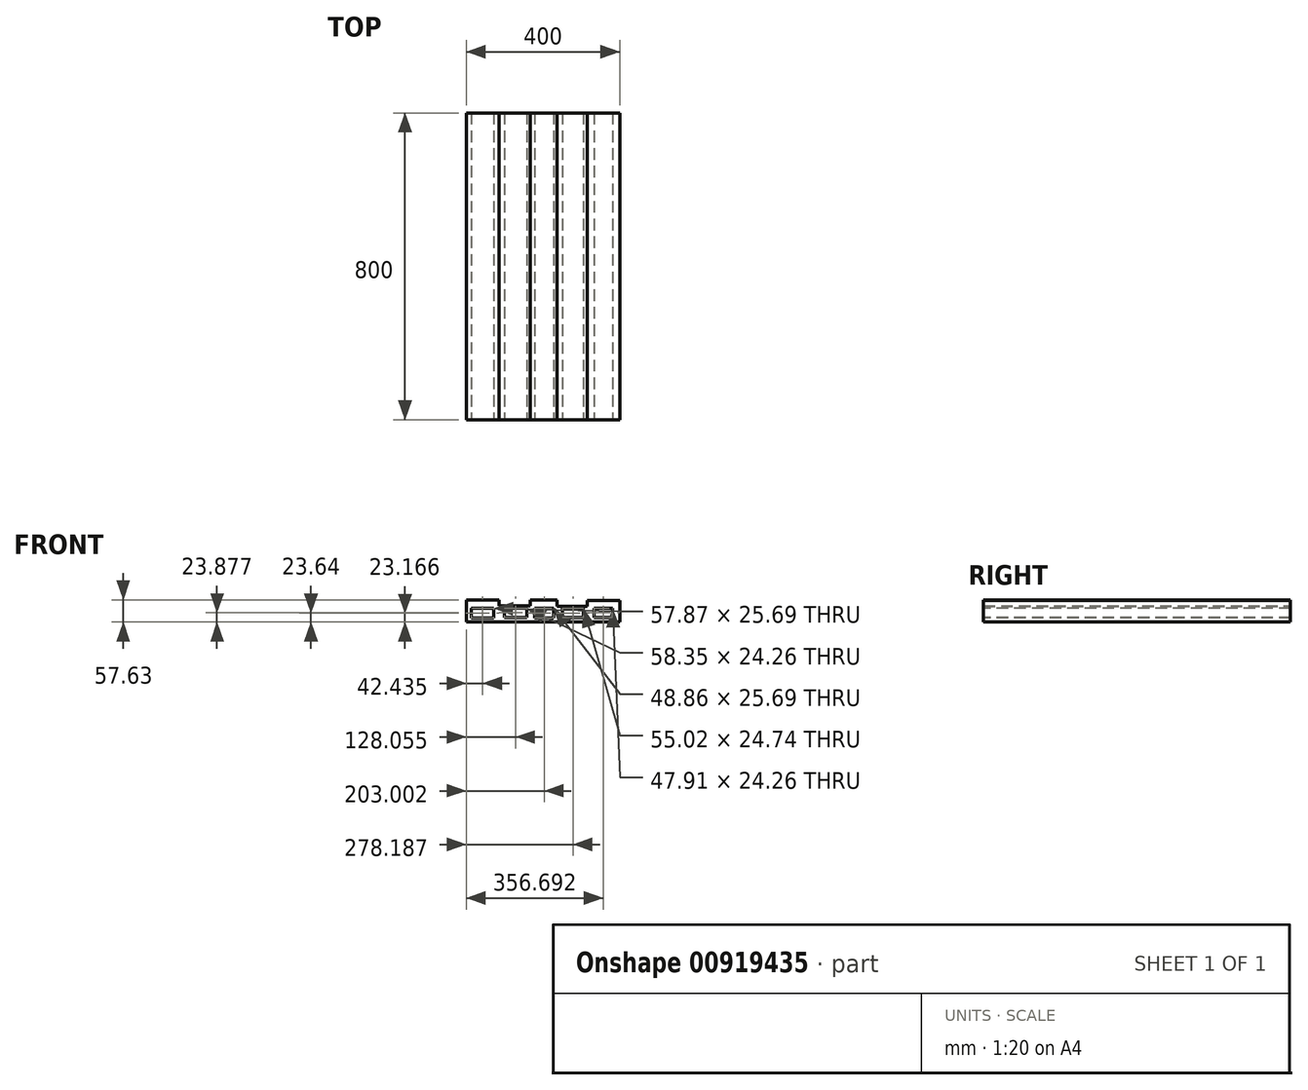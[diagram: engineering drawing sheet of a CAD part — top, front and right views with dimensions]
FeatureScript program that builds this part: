
annotation { "Feature Type Name" : "Feature", "Feature Type Description" : "" }
export const myFeature = defineFeature(function(context is Context, id is Id, definition is map)
    precondition{}
    {
        {
            var Q0;
            Q0=qCreatedBy(makeId("Front.planeOp"),FACE);
            var sketch = newSketch(context, id + "F0", { "sketchPlane" : qUnion([Q0])});
            skLineSegment(sketch, "E0.bottom", {"start": v(-56.77, 21.62) * mm, "end": v(28.15, 21.62) * mm});
            skLineSegment(sketch, "E0.top", {"start": v(-56.77, -36) * mm, "end": v(28.15, -36) * mm});
            skLineSegment(sketch, "E0.left", {"start": v(-56.77, 21.62) * mm, "end": v(-56.77, -36) * mm});
            skLineSegment(sketch, "E0.right", {"start": v(28.15, 21.62) * mm, "end": v(28.15, -36) * mm});
            skLineSegment(sketch, "E1.bottom", {"start": v(28.15, 5.48) * mm, "end": v(110.29, 5.48) * mm});
            skLineSegment(sketch, "E1.top", {"start": v(28.15, -36) * mm, "end": v(110.29, -36) * mm});
            skLineSegment(sketch, "E1.left", {"start": v(28.15, 5.48) * mm, "end": v(28.15, -36) * mm});
            skLineSegment(sketch, "E1.right", {"start": v(110.29, 5.48) * mm, "end": v(110.29, -36) * mm});
            skLineSegment(sketch, "E2.bottom", {"start": v(110.29, 21.62) * mm, "end": v(180.17, 21.62) * mm});
            skLineSegment(sketch, "E2.top", {"start": v(110.29, -36) * mm, "end": v(180.17, -36) * mm});
            skLineSegment(sketch, "E2.left", {"start": v(110.29, 21.62) * mm, "end": v(110.29, -36) * mm});
            skLineSegment(sketch, "E2.right", {"start": v(180.17, 21.62) * mm, "end": v(180.17, -36) * mm});
            skLineSegment(sketch, "E3.bottom", {"start": v(180.17, -36) * mm, "end": v(258.18, -36) * mm});
            skLineSegment(sketch, "E3.top", {"start": v(180.17, 4.79) * mm, "end": v(258.18, 4.79) * mm});
            skLineSegment(sketch, "E3.left", {"start": v(180.17, -36) * mm, "end": v(180.17, 4.79) * mm});
            skLineSegment(sketch, "E3.right", {"start": v(258.18, -36) * mm, "end": v(258.18, 4.79) * mm});
            skLineSegment(sketch, "E4.bottom", {"start": v(258.18, 19.75) * mm, "end": v(343.23, 19.75) * mm});
            skLineSegment(sketch, "E4.top", {"start": v(258.18, -36) * mm, "end": v(343.23, -36) * mm});
            skLineSegment(sketch, "E4.left", {"start": v(258.18, 19.75) * mm, "end": v(258.18, -36) * mm});
            skLineSegment(sketch, "E4.right", {"start": v(343.23, 19.75) * mm, "end": v(343.23, -36) * mm});
            skSolve(sketch);
        }
        {
            var Q0;
            Q0 = qSketchRegion(id + "F0", true);
            extrude(context, id + "F1", {"entities" : qUnion([Q0]), "depth" : 800 * mm, "offsetDistance" : 25 * mm});
        }
        {
            var Q0;
            Q0=makeQuery(id+"F1.opExtrude","CAP_FACE",FACE,{"disambiguationData":[OSD([sQuery(id+"F0.wireOp",EDGE,"E0.bottom"),sQuery(id+"F0.wireOp",EDGE,"E0.top"),sQuery(id+"F0.wireOp",EDGE,"E0.left"),sQuery(id+"F0.wireOp",EDGE,"E0.right"),sQuery(id+"F0.wireOp",EDGE,"E1.bottom"),sQuery(id+"F0.wireOp",EDGE,"E1.top"),sQuery(id+"F0.wireOp",EDGE,"E2.bottom"),sQuery(id+"F0.wireOp",EDGE,"E2.top"),sQuery(id+"F0.wireOp",EDGE,"E2.left"),sQuery(id+"F0.wireOp",EDGE,"E2.right"),sQuery(id+"F0.wireOp",EDGE,"E3.bottom"),sQuery(id+"F0.wireOp",EDGE,"E3.top"),sQuery(id+"F0.wireOp",EDGE,"E4.bottom"),sQuery(id+"F0.wireOp",EDGE,"E4.top"),sQuery(id+"F0.wireOp",EDGE,"E4.left"),sQuery(id+"F0.wireOp",EDGE,"E4.right")])],"isStart":false});
            var sketch = newSketch(context, id + "F2", { "sketchPlane" : qUnion([Q0])});
            skLineSegment(sketch, "E5.bottom", {"start": v(-43.27, 0) * mm, "end": v(14.6, 0) * mm});
            skLineSegment(sketch, "E5.top", {"start": v(-43.27, -25.69) * mm, "end": v(14.6, -25.69) * mm});
            skLineSegment(sketch, "E5.left", {"start": v(-43.27, 0) * mm, "end": v(-43.27, -25.69) * mm});
            skLineSegment(sketch, "E5.right", {"start": v(14.6, 0) * mm, "end": v(14.6, -25.69) * mm});
            skLineSegment(sketch, "E6.bottom", {"start": v(42.11, 0) * mm, "end": v(100.46, 0) * mm});
            skLineSegment(sketch, "E6.top", {"start": v(42.11, -24.26) * mm, "end": v(100.46, -24.26) * mm});
            skLineSegment(sketch, "E6.left", {"start": v(42.11, 0) * mm, "end": v(42.11, -24.26) * mm});
            skLineSegment(sketch, "E6.right", {"start": v(100.46, 0) * mm, "end": v(100.46, -24.26) * mm});
            skLineSegment(sketch, "E7.bottom", {"start": v(121.8, 0) * mm, "end": v(170.66, 0) * mm});
            skLineSegment(sketch, "E7.top", {"start": v(121.8, -25.69) * mm, "end": v(170.66, -25.69) * mm});
            skLineSegment(sketch, "E7.left", {"start": v(121.8, 0) * mm, "end": v(121.8, -25.69) * mm});
            skLineSegment(sketch, "E7.right", {"start": v(170.66, 0) * mm, "end": v(170.66, -25.69) * mm});
            skLineSegment(sketch, "E8.bottom", {"start": v(193.9, 0) * mm, "end": v(248.93, 0) * mm});
            skLineSegment(sketch, "E8.top", {"start": v(193.9, -24.74) * mm, "end": v(248.93, -24.74) * mm});
            skLineSegment(sketch, "E8.left", {"start": v(193.9, 0) * mm, "end": v(193.9, -24.74) * mm});
            skLineSegment(sketch, "E8.right", {"start": v(248.93, 0) * mm, "end": v(248.93, -24.74) * mm});
            skLineSegment(sketch, "E9.bottom", {"start": v(275.97, 0) * mm, "end": v(323.88, 0) * mm});
            skLineSegment(sketch, "E9.top", {"start": v(275.97, -24.26) * mm, "end": v(323.88, -24.26) * mm});
            skLineSegment(sketch, "E9.left", {"start": v(275.97, 0) * mm, "end": v(275.97, -24.26) * mm});
            skLineSegment(sketch, "E9.right", {"start": v(323.88, 0) * mm, "end": v(323.88, -24.26) * mm});
            skSolve(sketch);
        }
        {
            var Q0;
            Q0 = qSketchRegion(id + "F2", true);
            extrude(context, id + "F3", {"entities" : qUnion([Q0]), "operationType" : NewBodyOperationType.REMOVE, "endBound" : BoundingType.UP_TO_NEXT, "oppositeDirection" : true, "depth" : 25 * mm, "offsetDistance" : 25 * mm});
        }
    });
